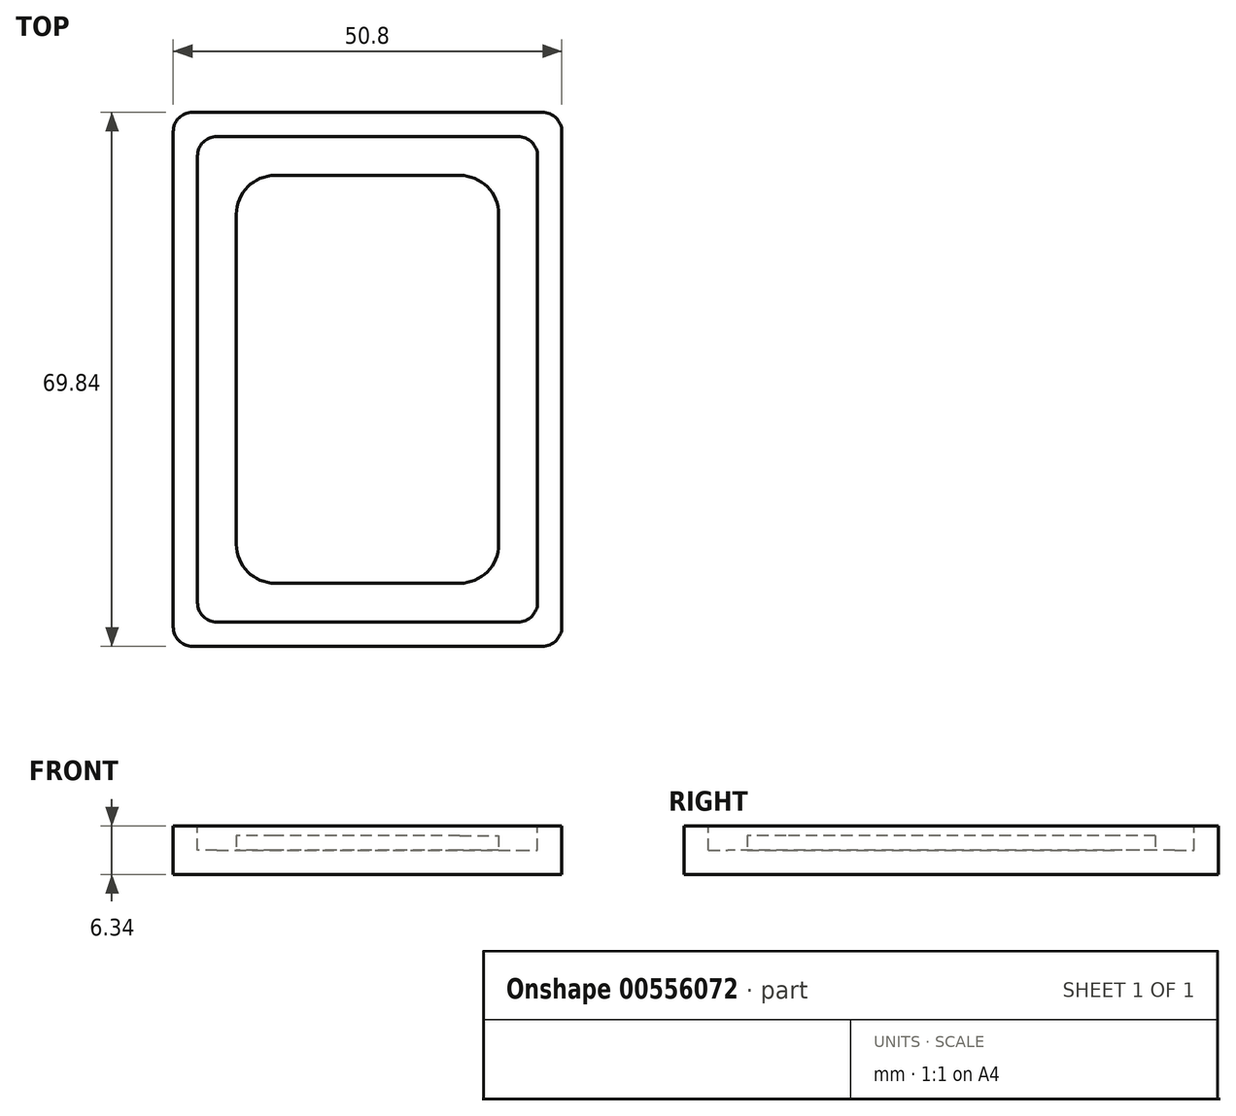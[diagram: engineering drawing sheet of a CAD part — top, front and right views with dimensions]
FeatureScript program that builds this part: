
annotation { "Feature Type Name" : "Feature", "Feature Type Description" : "" }
export const myFeature = defineFeature(function(context is Context, id is Id, definition is map)
    precondition{}
    {
        {
            var Q0;
            Q0=qCreatedBy(makeId("Top.planeOp"),FACE);
            var sketch = newSketch(context, id + "F0", { "sketchPlane" : qUnion([Q0])});
            skLineSegment(sketch, "E0.bottom", {"start": v(25.4, 34.93) * mm, "end": v(-25.4, 34.93) * mm});
            skLineSegment(sketch, "E0.top", {"start": v(25.4, -34.93) * mm, "end": v(-25.4, -34.93) * mm});
            skLineSegment(sketch, "E0.left", {"start": v(25.4, 34.93) * mm, "end": v(25.4, -34.93) * mm});
            skLineSegment(sketch, "E0.right", {"start": v(-25.4, 34.93) * mm, "end": v(-25.4, -34.93) * mm});
            skPoint(sketch, "E0.middle", {"position": v(0, 0) * mm});
            skSolve(sketch);
        }
        {
            var Q0;
            Q0=makeQuery(id+"F0.imprint","IMPRINT",FACE,{"disambiguationData":[TD([[makeQuery(id+"F0.imprint","IMPRINT",EDGE,{"derivedFrom":sQuery(id+"F0.wireOp",EDGE,"E0.bottom")}),1.0]])]});
            extrude(context, id + "F1", {"entities" : qUnion([Q0]), "endBound" : BoundingType.SYMMETRIC, "oppositeDirection" : true, "depth" : 6.35 * mm, "offsetDistance" : 25.4 * mm});
        }
        {
            var Q0;
            Q0=makeQuery(id+"F1.opExtrude","SWEPT_EDGE",EDGE,{"disambiguationData":[OSD([sQuery(id+"F0.wireOp",EDGE,"E0.top"),sQuery(id+"F0.wireOp",EDGE,"E0.left")])]});
            var Q1;
            Q1=makeQuery(id+"F1.opExtrude","SWEPT_EDGE",EDGE,{"disambiguationData":[OSD([sQuery(id+"F0.wireOp",EDGE,"E0.top"),sQuery(id+"F0.wireOp",EDGE,"E0.right")])]});
            var Q2;
            Q2=makeQuery(id+"F1.opExtrude","SWEPT_EDGE",EDGE,{"disambiguationData":[OSD([sQuery(id+"F0.wireOp",EDGE,"E0.bottom"),sQuery(id+"F0.wireOp",EDGE,"E0.left")])]});
            var Q3;
            Q3=makeQuery(id+"F1.opExtrude","SWEPT_EDGE",EDGE,{"disambiguationData":[OSD([sQuery(id+"F0.wireOp",EDGE,"E0.bottom"),sQuery(id+"F0.wireOp",EDGE,"E0.right")])]});
            fillet(context, id + "F2", {"entities" : qUnion([Q0, Q1, Q2, Q3]), "radius" : 2.54 * mm, "tangentPropagation" : true, "allowEdgeOverflow" : false});
        }
        {
            var Q0;
            Q0=makeQuery(id+"F1.opExtrude","CAP_FACE",FACE,{"disambiguationData":[OSD([sQuery(id+"F0.wireOp",EDGE,"E0.bottom"),sQuery(id+"F0.wireOp",EDGE,"E0.top"),sQuery(id+"F0.wireOp",EDGE,"E0.left"),sQuery(id+"F0.wireOp",EDGE,"E0.right")])],"isStart":true});
            var sketch = newSketch(context, id + "F3", { "sketchPlane" : qUnion([Q0])});
            skLineSegment(sketch, "E1.0.0", {"start": v(-22.86, -34.93) * mm, "end": v(22.86, -34.93) * mm});
            skArc(sketch, "E1.0.1", {"start": v(22.86, -34.93) * mm, "mid": v(24.66, -34.18) * mm, "end": v(25.4, -32.39) * mm});
            skLineSegment(sketch, "E1.0.2", {"start": v(25.4, -32.39) * mm, "end": v(25.4, 32.38) * mm});
            skArc(sketch, "E1.0.3", {"start": v(25.4, 32.38) * mm, "mid": v(24.66, 34.18) * mm, "end": v(22.86, 34.92) * mm});
            skLineSegment(sketch, "E1.0.4", {"start": v(22.86, 34.93) * mm, "end": v(-22.86, 34.93) * mm});
            skArc(sketch, "E1.0.5", {"start": v(-22.86, 34.93) * mm, "mid": v(-24.66, 34.18) * mm, "end": v(-25.4, 32.39) * mm});
            skLineSegment(sketch, "E1.0.6", {"start": v(-25.4, 32.39) * mm, "end": v(-25.4, -32.38) * mm});
            skArc(sketch, "E1.0.7", {"start": v(-25.4, -32.38) * mm, "mid": v(-24.66, -34.18) * mm, "end": v(-22.86, -34.92) * mm});
            skLineSegment(sketch, "E2.0", {"start": v(-22.23, -31.75) * mm, "end": v(22.22, -31.75) * mm});
            skLineSegment(sketch, "E2.1", {"start": v(-22.22, 31.75) * mm, "end": v(-22.23, -31.75) * mm});
            skLineSegment(sketch, "E2.2", {"start": v(22.23, 31.75) * mm, "end": v(-22.22, 31.75) * mm});
            skLineSegment(sketch, "E2.3", {"start": v(22.22, -31.75) * mm, "end": v(22.23, 31.75) * mm});
            skSolve(sketch);
        }
        {
            var Q0;
            Q0=makeQuery(id+"F3.imprint","IMPRINT",FACE,{"disambiguationData":[TD([[makeQuery(id+"F3.imprint","IMPRINT",EDGE,{"derivedFrom":sQuery(id+"F3.wireOp",EDGE,"E2.0")}),1.0]])]});
            extrude(context, id + "F4", {"entities" : qUnion([Q0]), "operationType" : NewBodyOperationType.REMOVE, "oppositeDirection" : true, "depth" : 3.17 * mm, "offsetDistance" : 25.4 * mm});
        }
        {
            var Q0;
            Q0=makeQuery(id+"F4.boolean.opBoolean","COPY",EDGE,{"derivedFrom":makeQuery(id+"F4.opExtrude","SWEPT_EDGE",EDGE,{"disambiguationData":[OSD([sQuery(id+"F3.wireOp",EDGE,"E2.1"),sQuery(id+"F3.wireOp",EDGE,"E2.2")])]})});
            var Q1;
            Q1=makeQuery(id+"F4.boolean.opBoolean","COPY",EDGE,{"derivedFrom":makeQuery(id+"F4.opExtrude","SWEPT_EDGE",EDGE,{"disambiguationData":[OSD([sQuery(id+"F3.wireOp",EDGE,"E2.2"),sQuery(id+"F3.wireOp",EDGE,"E2.3")])]})});
            var Q2;
            Q2=makeQuery(id+"F4.boolean.opBoolean","COPY",EDGE,{"derivedFrom":makeQuery(id+"F4.opExtrude","SWEPT_EDGE",EDGE,{"disambiguationData":[OSD([sQuery(id+"F3.wireOp",EDGE,"E2.0"),sQuery(id+"F3.wireOp",EDGE,"E2.1")])]})});
            var Q3;
            Q3=makeQuery(id+"F4.boolean.opBoolean","COPY",EDGE,{"derivedFrom":makeQuery(id+"F4.opExtrude","SWEPT_EDGE",EDGE,{"disambiguationData":[OSD([sQuery(id+"F3.wireOp",EDGE,"E2.0"),sQuery(id+"F3.wireOp",EDGE,"E2.3")])]})});
            fillet(context, id + "F5", {"entities" : qUnion([Q0, Q1, Q2, Q3]), "radius" : 2.54 * mm, "tangentPropagation" : true, "allowEdgeOverflow" : false});
        }
        {
            var Q0;
            Q0=makeQuery(id+"F4.boolean.opBoolean","COPY",FACE,{"derivedFrom":makeQuery(id+"F4.opExtrude","CAP_FACE",FACE,{"disambiguationData":[OSD([sQuery(id+"F3.wireOp",EDGE,"E2.0"),sQuery(id+"F3.wireOp",EDGE,"E2.1"),sQuery(id+"F3.wireOp",EDGE,"E2.2"),sQuery(id+"F3.wireOp",EDGE,"E2.3")])],"isStart":false})});
            var sketch = newSketch(context, id + "F6", { "sketchPlane" : qUnion([Q0])});
            skLineSegment(sketch, "E3.0", {"start": v(-12.07, -26.67) * mm, "end": v(12.06, -26.67) * mm});
            skLineSegment(sketch, "E3.1", {"start": v(-17.14, 21.6) * mm, "end": v(-17.15, -21.6) * mm});
            skLineSegment(sketch, "E3.2", {"start": v(12.07, 26.67) * mm, "end": v(-12.06, 26.67) * mm});
            skLineSegment(sketch, "E3.3", {"start": v(17.14, -21.6) * mm, "end": v(17.15, 21.6) * mm});
            skPoint(sketch, "E4.visualSharp", {"position": v(-17.14, 26.67) * mm});
            skArc(sketch, "E4.filletArc", {"start": v(-12.06, 26.67) * mm, "mid": v(-15.66, 25.18) * mm, "end": v(-17.14, 21.6) * mm});
            skPoint(sketch, "E5.visualSharp", {"position": v(17.15, 26.67) * mm});
            skArc(sketch, "E5.filletArc", {"start": v(17.15, 21.6) * mm, "mid": v(15.66, 25.18) * mm, "end": v(12.07, 26.67) * mm});
            skPoint(sketch, "E6.visualSharp", {"position": v(-17.15, -26.67) * mm});
            skArc(sketch, "E6.filletArc", {"start": v(-17.15, -21.6) * mm, "mid": v(-15.66, -25.18) * mm, "end": v(-12.07, -26.67) * mm});
            skPoint(sketch, "E7.visualSharp", {"position": v(17.14, -26.67) * mm});
            skArc(sketch, "E7.filletArc", {"start": v(12.06, -26.67) * mm, "mid": v(15.66, -25.18) * mm, "end": v(17.14, -21.6) * mm});
            skSolve(sketch);
        }
        {
            var Q0;
            Q0=makeQuery(id+"F6.imprint","IMPRINT",FACE,{"disambiguationData":[TD([[makeQuery(id+"F6.imprint","IMPRINT",EDGE,{"derivedFrom":sQuery(id+"F6.wireOp",EDGE,"E3.0")}),1.0]])]});
            extrude(context, id + "F7", {"entities" : qUnion([Q0]), "operationType" : NewBodyOperationType.ADD, "depth" : 1.9 * mm, "offsetDistance" : 25.4 * mm});
        }
    });
